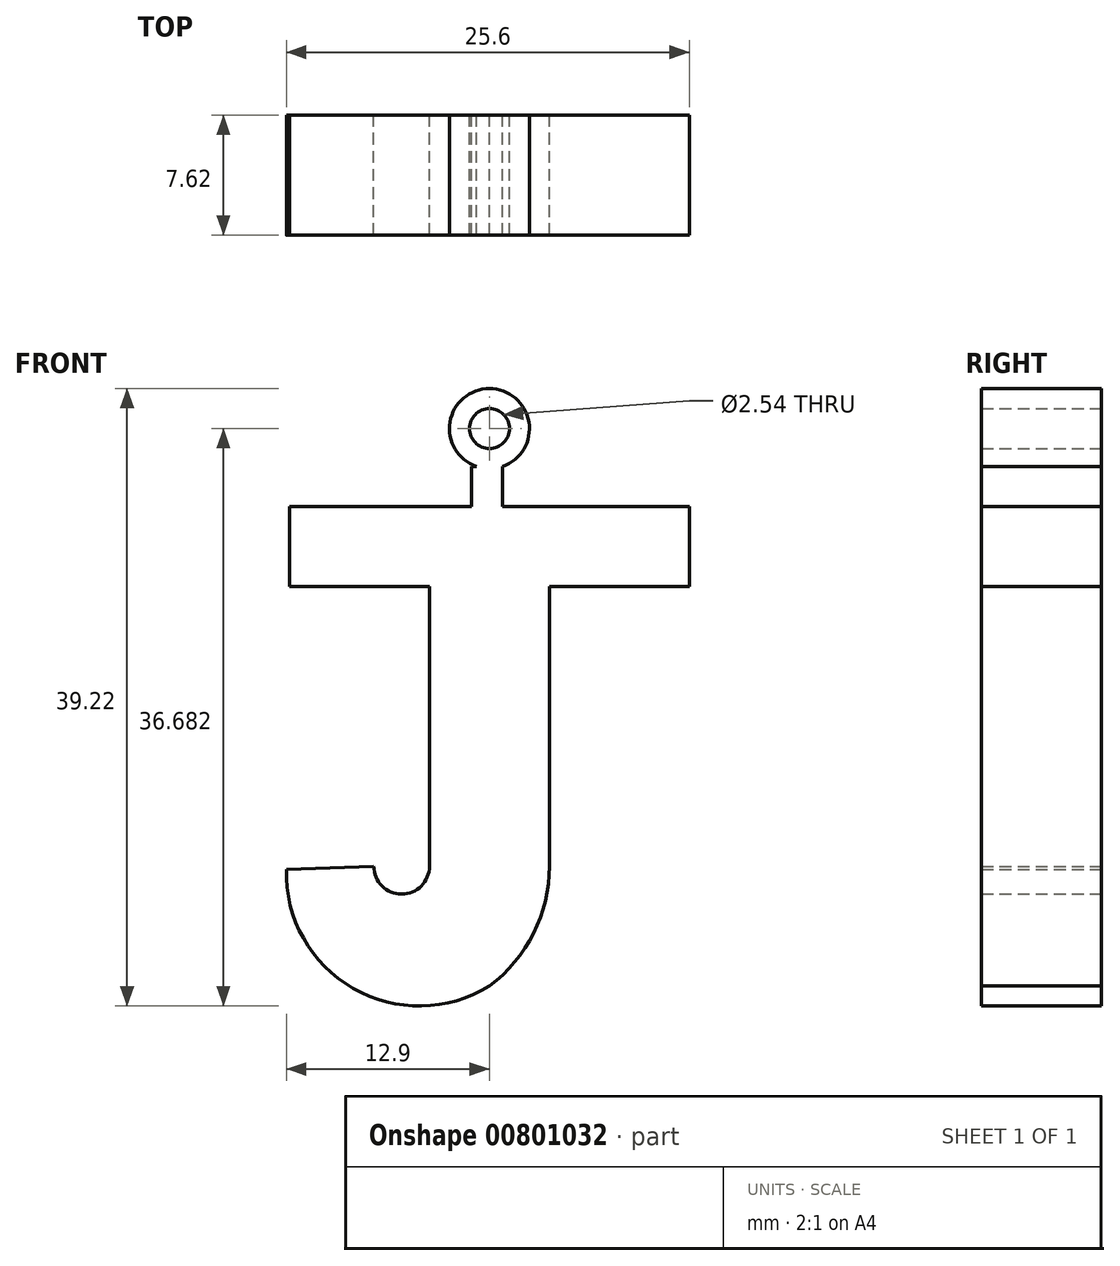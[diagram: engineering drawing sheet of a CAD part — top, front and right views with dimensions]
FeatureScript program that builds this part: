
annotation { "Feature Type Name" : "Feature", "Feature Type Description" : "" }
export const myFeature = defineFeature(function(context is Context, id is Id, definition is map)
    precondition{}
    {
        {
            var Q0;
            Q0=qCreatedBy(makeId("Front.planeOp"),FACE);
            var sketch = newSketch(context, id + "F0", { "sketchPlane" : qUnion([Q0])});
            skLineSegment(sketch, "E0", {"start": v(0, 0) * mm, "end": v(12.7, 0) * mm});
            skLineSegment(sketch, "E1", {"start": v(0, 0) * mm, "end": v(-12.7, 0) * mm});
            skLineSegment(sketch, "E2", {"start": v(12.7, 0) * mm, "end": v(12.7, -5.08) * mm});
            skLineSegment(sketch, "E3", {"start": v(-12.7, -5.08) * mm, "end": v(-12.7, 0) * mm});
            skLineSegment(sketch, "E4", {"start": v(-12.7, -5.08) * mm, "end": v(-3.81, -5.08) * mm});
            skLineSegment(sketch, "E5", {"start": v(12.7, -5.08) * mm, "end": v(3.81, -5.08) * mm});
            skLineSegment(sketch, "E6", {"start": v(3.81, -5.08) * mm, "end": v(3.81, -22.86) * mm});
            skLineSegment(sketch, "E7", {"start": v(-3.81, -5.08) * mm, "end": v(-3.8, -22.86) * mm});
            skArc(sketch, "E8", {"start": v(0, -30.46) * mm, "mid": v(2.8, -27.11) * mm, "end": v(3.81, -22.86) * mm});
            skArc(sketch, "E9", {"start": v(-12.9, -23.07) * mm, "mid": v(-8.66, -30.62) * mm, "end": v(0, -30.46) * mm});
            skArc(sketch, "E10", {"start": v(-7.35, -22.86) * mm, "mid": v(-5.58, -24.63) * mm, "end": v(-3.8, -22.86) * mm});
            skLineSegment(sketch, "E11", {"start": v(-12.9, -23.07) * mm, "end": v(-7.35, -22.86) * mm});
            skLineSegment(sketch, "E12.bottom", {"start": v(-1.12, 2.54) * mm, "end": v(0.82, 2.54) * mm});
            skLineSegment(sketch, "E12.top", {"start": v(-1.12, 0) * mm, "end": v(0.82, 0) * mm});
            skLineSegment(sketch, "E12.left", {"start": v(-1.12, 2.54) * mm, "end": v(-1.12, 0) * mm});
            skLineSegment(sketch, "E12.right", {"start": v(0.82, 2.54) * mm, "end": v(0.82, 0) * mm});
            skCircle(sketch, "E13", {"center": v(0, 4.94) * mm, "radius": 2.54 * mm});
            skCircle(sketch, "E14", {"center": v(0, 4.94) * mm, "radius": 0.59 * mm});
            skCircle(sketch, "E15", {"center": v(0, 4.94) * mm, "radius": 1.27 * mm});
            skSolve(sketch);
        }
        {
            var Q0;
            Q0 = qSketchRegion(id + "F0", true);
            extrude(context, id + "F1", {"entities" : qUnion([Q0]), "depth" : 7.62 * mm, "offsetDistance" : 25.4 * mm});
        }
    });
